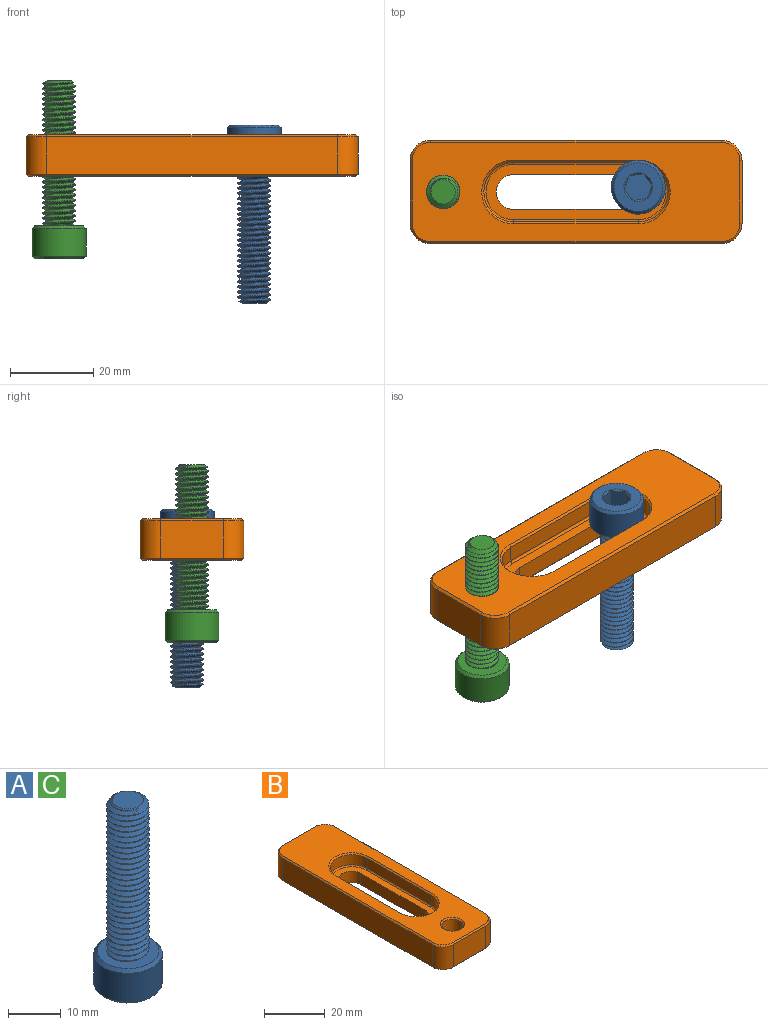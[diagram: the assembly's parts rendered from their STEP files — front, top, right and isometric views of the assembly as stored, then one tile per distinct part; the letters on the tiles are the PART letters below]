
ASSEMBLY  parts=3 mates=2
PART A: 24 faces, bbox 14.3x14.3x44.8 mm
  f0: cylinder r=4mm len=34.25mm, axis (0,0,1), area 212.7mm2, adj f1,f2,f4,f8
  f1: bspline ~36.09x9.24mm, area 588.2mm2, adj f0,f3,f4,f8
  f2: bspline ~35.47x9.24mm, area 584.3mm2, adj f0,f3,f4,f8
  f3: cylinder r=3.19mm len=34.82mm, axis (0,0,-1), area 206.8mm2, adj f1,f2,f4,f8
  f4: cone r=2.93mm half-angle=55deg, axis (0,0,-1), area 16.8mm2, adj f0,f1,f2,f3,f5
  f5: plane 5.87x5.87mm, normal (0,0,1), area 27mm2, adj f4
  f6: cylinder r=6.5mm len=13mm, axis (0,0,1), area 273.6mm2, adj f22,f23
  f7: plane 11.7x11.7mm, normal (0,0,-1), area 69.8mm2, adj f9,f10,f11,f12,f13,f14,f22
  f8: plane 12.2x12.2mm, normal (0,0,1), area 66.7mm2, adj f0,f1,f2,f3,f23
  f9: cone r=3.46mm half-angle=45deg, axis (0,0,-1), area 0mm2, adj f7,f16
  f10: cone r=3.46mm half-angle=45deg, axis (0,0,-1), area 0mm2, adj f7,f17
  f11: cone r=3.46mm half-angle=45deg, axis (0,0,-1), area 0mm2, adj f7,f18
  f12: cone r=3.46mm half-angle=45deg, axis (0,0,-1), area 0mm2, adj f7,f19
  f13: cone r=3.46mm half-angle=45deg, axis (0,0,-1), area 0mm2, adj f7,f20
  f14: cone r=3.46mm half-angle=45deg, axis (0,0,-1), area 0mm2, adj f7,f21
  f15: plane 6.93x6mm, normal (0,0,-1), area 31.2mm2, adj f16,f17,f18,f19,f20,f21
  f16: plane 5.81x4.31mm, normal (-0.5,-0.87,0), area 14.5mm2, adj f9,f15,f17,f21
  f17: plane 5.82x4.78mm, normal (-1,0,0), area 14.5mm2, adj f10,f15,f16,f18
  f18: plane 5.81x4.31mm, normal (-0.5,0.87,0), area 14.5mm2, adj f11,f15,f17,f19
  f19: plane 5.81x4.31mm, normal (0.5,0.87,0), area 14.5mm2, adj f12,f15,f18,f20
  f20: plane 5.82x4.78mm, normal (1,0,0), area 14.5mm2, adj f13,f15,f19,f21
  f21: plane 5.81x4.31mm, normal (0.5,-0.87,0), area 14.5mm2, adj f14,f15,f16,f20
  f22: cone r=5.85mm half-angle=45deg, axis (0,0,1), area 35.7mm2, adj f6,f7
  f23: cone r=6.5mm half-angle=45deg, axis (0,0,-1), area 35.7mm2, adj f6,f8
PART B: 50 faces, bbox 25x80x10 mm
  f0: plane 30x4.5mm, normal (-1,0,0), area 135mm2, adj f2,f3,f15,f32
  f1: plane 30x4.5mm, normal (1,0,0), area 135mm2, adj f2,f3,f15,f29
  f2: cylinder r=4.2mm len=8.4mm, axis (0,0,-1), area 59.4mm2, adj f0,f1,f15,f30
  f3: cylinder r=4.2mm len=8.4mm, axis (0,0,-1), area 59.4mm2, adj f0,f1,f15,f31
  f4: plane 79x24mm, normal (0,0,1), area 1180.1mm2, adj f33,f34,f35,f36,f37,f38,f39,f40
  f5: plane 70x9mm, normal (-1,0,0), area 630mm2, adj f16,f19,f20,f33
  f6: plane 15x9mm, normal (0,-1,0), area 135mm2, adj f16,f17,f24,f37
  f7: plane 70x9mm, normal (1,0,0), area 630mm2, adj f17,f18,f27,f40
  f8: cylinder r=3.5mm len=9mm, axis (0,0,-1), area 197.9mm2, adj f28,f45
  f9: plane 15x9mm, normal (0,1,0), area 135mm2, adj f18,f19,f23,f36
  f10: plane 79x24mm, normal (0,0,-1), area 1477mm2, adj f20,f21,f22,f23,f24,f25,f26,f27
  f11: cylinder r=7.2mm len=14.4mm, axis (0,0,1), area 90.5mm2, adj f12,f14,f44,f49
  f12: plane 30x4mm, normal (-1,0,0), area 120mm2, adj f11,f13,f42,f47
  f13: cylinder r=7.2mm len=14.4mm, axis (0,0,1), area 90.5mm2, adj f12,f14,f41,f46
  f14: plane 30x4mm, normal (1,0,0), area 120mm2, adj f11,f13,f43,f48
  f15: plane 43.4x13.4mm, normal (0,0,1), area 235.6mm2, adj f0,f1,f2,f3,f46,f47,f48,f49
  f16: cylinder r=5mm len=9mm, axis (0,0,-1), area 70.7mm2, adj f5,f6,f22,f35
  f17: cylinder r=5mm len=9mm, axis (0,0,1), area 70.7mm2, adj f6,f7,f26,f39
  f18: cylinder r=5mm len=9mm, axis (0,0,-1), area 70.7mm2, adj f7,f9,f25,f38
  f19: cylinder r=5mm len=9mm, axis (0,0,1), area 70.7mm2, adj f5,f9,f21,f34
  f20: plane 70x0.5mm, normal (-0.71,0,-0.71), area 49.5mm2, adj f5,f10,f21,f22
  f21: cone r=4.5mm half-angle=45deg, axis (0,0,1), area 5.3mm2, adj f10,f19,f20,f23
  f22: cone r=4.5mm half-angle=45deg, axis (0,0,1), area 5.3mm2, adj f10,f16,f20,f24
  f23: plane 15x0.5mm, normal (0,0.71,-0.71), area 10.6mm2, adj f9,f10,f21,f25
  f24: plane 15x0.5mm, normal (0,-0.71,-0.71), area 10.6mm2, adj f6,f10,f22,f26
  f25: cone r=4.5mm half-angle=45deg, axis (0,0,1), area 5.3mm2, adj f10,f18,f23,f27
  f26: cone r=4.5mm half-angle=45deg, axis (0,0,1), area 5.3mm2, adj f10,f17,f24,f27
  f27: plane 70x0.5mm, normal (0.71,0,-0.71), area 49.5mm2, adj f7,f10,f25,f26
  f28: cone r=4mm half-angle=45deg, axis (0,0,-1), area 16.7mm2, adj f8,f10
  f29: plane 30x0.5mm, normal (0.71,0,-0.71), area 21.2mm2, adj f1,f10,f30,f31
  f30: cone r=4.7mm half-angle=45deg, axis (0,0,-1), area 9.9mm2, adj f2,f10,f29,f32
  f31: cone r=4.2mm half-angle=45deg, axis (0,0,-1), area 9.9mm2, adj f3,f10,f29,f32
  f32: plane 30x0.5mm, normal (-0.71,0,-0.71), area 21.2mm2, adj f0,f10,f30,f31
  f33: plane 70x0.5mm, normal (-0.71,0,0.71), area 49.5mm2, adj f4,f5,f34,f35
  f34: cone r=4.5mm half-angle=45deg, axis (0,0,-1), area 5.3mm2, adj f4,f19,f33,f36
  f35: cone r=4.5mm half-angle=45deg, axis (0,0,-1), area 5.3mm2, adj f4,f16,f33,f37
  f36: plane 15x0.5mm, normal (0,0.71,0.71), area 10.6mm2, adj f4,f9,f34,f38
  f37: plane 15x0.5mm, normal (0,-0.71,0.71), area 10.6mm2, adj f4,f6,f35,f39
  f38: cone r=4.5mm half-angle=45deg, axis (0,0,-1), area 5.3mm2, adj f4,f18,f36,f40
  f39: cone r=4.5mm half-angle=45deg, axis (0,0,-1), area 5.3mm2, adj f4,f17,f37,f40
  f40: plane 70x0.5mm, normal (0.71,0,0.71), area 49.5mm2, adj f4,f7,f38,f39
  f41: cone r=7.2mm half-angle=45deg, axis (0,0,1), area 16.5mm2, adj f4,f13,f42,f43
  f42: plane 30x0.5mm, normal (-0.71,0,0.71), area 21.2mm2, adj f4,f12,f41,f44
  f43: plane 30x0.5mm, normal (0.71,0,0.71), area 21.2mm2, adj f4,f14,f41,f44
  f44: cone r=7.7mm half-angle=45deg, axis (0,0,1), area 16.5mm2, adj f4,f11,f42,f43
  f45: cone r=3.5mm half-angle=45deg, axis (0,0,1), area 16.7mm2, adj f4,f8
  f46: torus R=6.7mm, axis (0,0,1), area 17.3mm2, adj f13,f15,f47,f48
  f47: cylinder r=0.5mm len=30mm, axis (0,1,0), area 23.6mm2, adj f12,f15,f46,f49
  f48: cylinder r=0.5mm len=30mm, axis (0,-1,0), area 23.6mm2, adj f14,f15,f46,f49
  f49: torus R=6.7mm, axis (0,0,1), area 17.3mm2, adj f11,f15,f47,f48
PART C: same geometry as A
PLACE A rot(axis=(0.33,-0.94,0),180deg) t=(16.63,1.6,-30.65)mm
PLACE B rot(axis=(0,0,-1),90deg) t=(1.63,0.44,0)mm fixed
PLACE C rot(axis=(0,0,-1),90deg) t=(-30.37,0.44,23.07)mm
MATE pin_slot A.f0 <-> B.f2  axis (0,0,1) through (16.63,1.6,5)mm
MATE slider C.f0 <-> B.f8  axis (0,0,-1) through (-30.37,0.44,-12.58)mm
